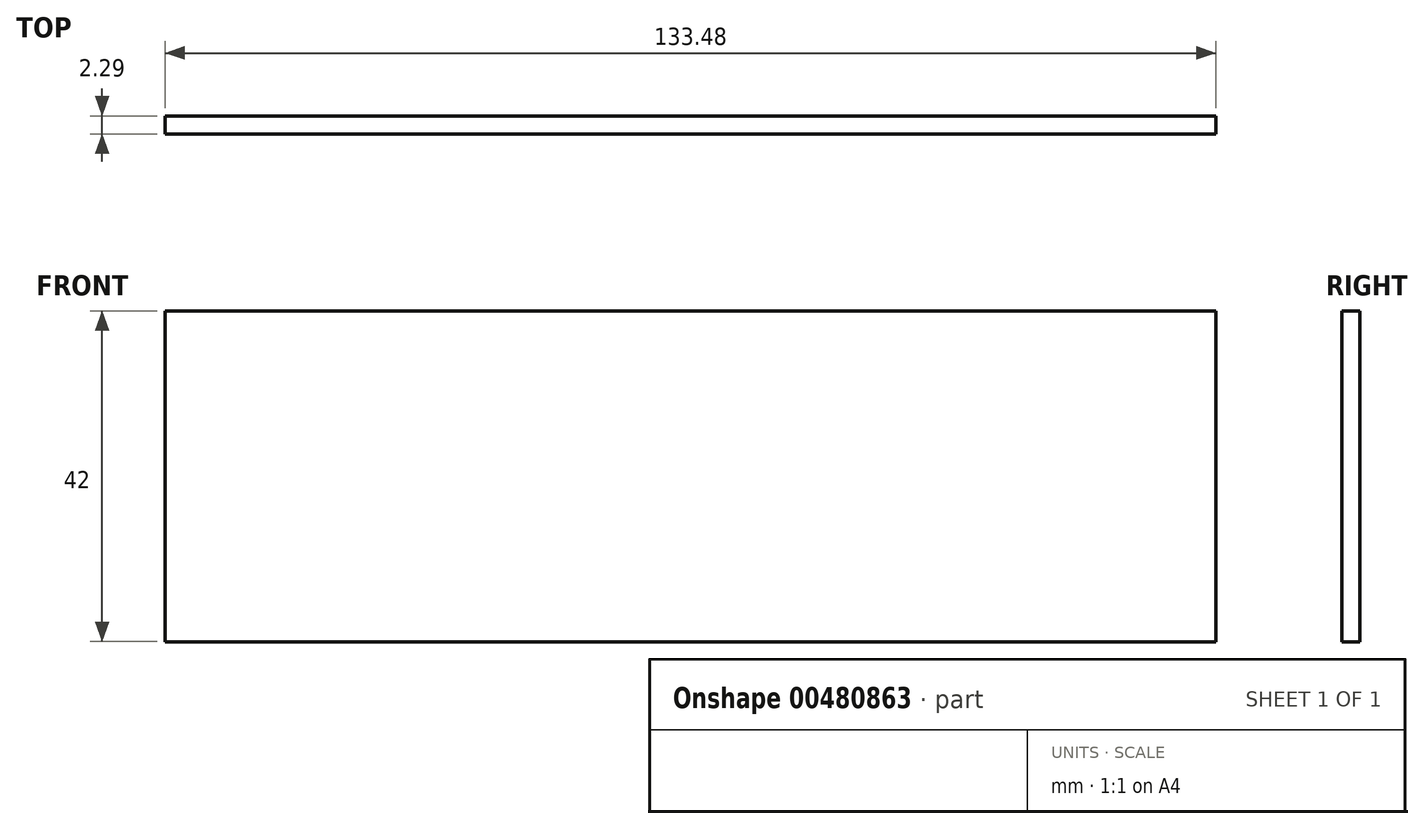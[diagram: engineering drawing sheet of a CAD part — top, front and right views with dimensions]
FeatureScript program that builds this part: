
annotation { "Feature Type Name" : "Feature", "Feature Type Description" : "" }
export const myFeature = defineFeature(function(context is Context, id is Id, definition is map)
    precondition{}
    {
        {
            var Q0;
            Q0=qCreatedBy(makeId("Front.planeOp"),FACE);
            var sketch = newSketch(context, id + "F0", { "sketchPlane" : qUnion([Q0])});
            skLineSegment(sketch, "E0.bottom", {"start": v(-66.74, -21) * mm, "end": v(66.74, -21) * mm});
            skLineSegment(sketch, "E0.top", {"start": v(-66.74, 21) * mm, "end": v(66.74, 21) * mm});
            skLineSegment(sketch, "E0.left", {"start": v(-66.74, -21) * mm, "end": v(-66.74, 21) * mm});
            skLineSegment(sketch, "E0.right", {"start": v(66.74, -21) * mm, "end": v(66.74, 21) * mm});
            skPoint(sketch, "E0.middle", {"position": v(0, 0) * mm});
            skSolve(sketch);
        }
        {
            var Q0;
            Q0=makeQuery(id+"F0.imprint","IMPRINT",FACE,{"disambiguationData":[TD([[makeQuery(id+"F0.imprint","IMPRINT",EDGE,{"derivedFrom":sQuery(id+"F0.wireOp",EDGE,"E0.bottom")}),1.0]])]});
            extrude(context, id + "F1", {"entities" : qUnion([Q0]), "depth" : 2.3 * mm});
        }
    });
